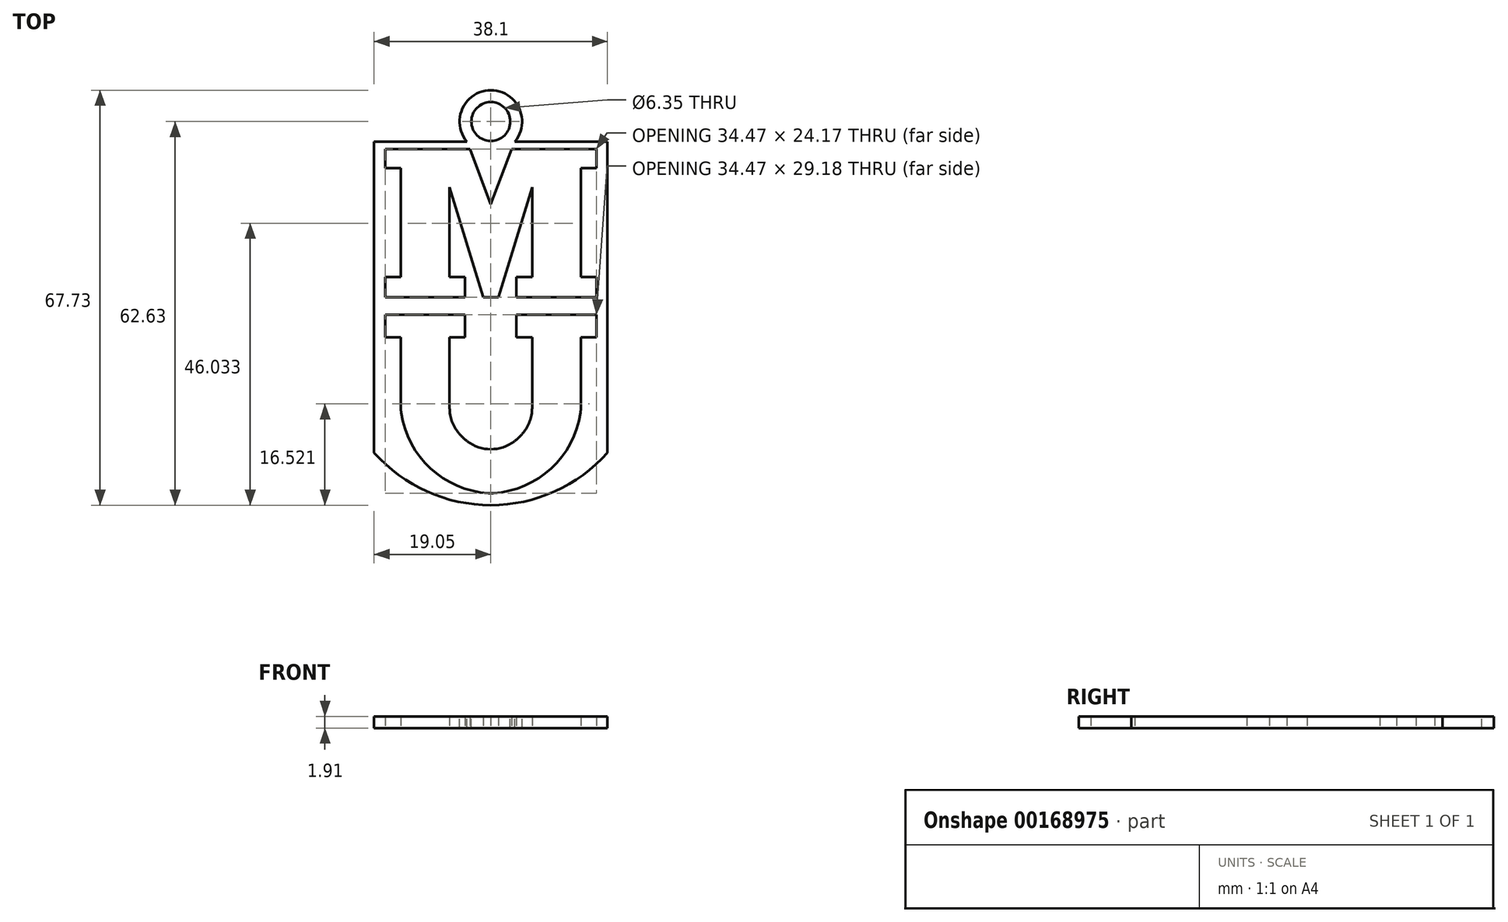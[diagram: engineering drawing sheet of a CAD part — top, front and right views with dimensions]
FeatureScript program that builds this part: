
annotation { "Feature Type Name" : "Feature", "Feature Type Description" : "" }
export const myFeature = defineFeature(function(context is Context, id is Id, definition is map)
    precondition{}
    {
        {
            var Q0;
            Q0=qCreatedBy(makeId("Top.planeOp"),FACE);
            var sketch = newSketch(context, id + "F0", { "sketchPlane" : qUnion([Q0])});
            skLineSegment(sketch, "E0.0.0", {"start": v(-17.24, 0) * mm, "end": v(-4.2, 0) * mm});
            skLineSegment(sketch, "E0.0.1", {"start": v(-4.2, 0) * mm, "end": v(-4.2, 3.32) * mm});
            skLineSegment(sketch, "E0.0.2", {"start": v(-4.2, 3.32) * mm, "end": v(-6.73, 3.32) * mm});
            skLineSegment(sketch, "E0.0.3", {"start": v(-6.73, 3.32) * mm, "end": v(-6.73, 17.94) * mm});
            skLineSegment(sketch, "E0.0.4", {"start": v(-6.73, 17.94) * mm, "end": v(-1.23, 0) * mm});
            skLineSegment(sketch, "E0.0.5", {"start": v(-1.23, 0) * mm, "end": v(1.23, 0) * mm});
            skLineSegment(sketch, "E0.0.6", {"start": v(1.23, 0) * mm, "end": v(6.73, 17.94) * mm});
            skLineSegment(sketch, "E0.0.7", {"start": v(6.73, 17.94) * mm, "end": v(6.73, 3.32) * mm});
            skLineSegment(sketch, "E0.0.8", {"start": v(6.73, 3.32) * mm, "end": v(4.2, 3.32) * mm});
            skLineSegment(sketch, "E0.0.9", {"start": v(4.2, 3.32) * mm, "end": v(4.2, 0) * mm});
            skLineSegment(sketch, "E0.0.10", {"start": v(4.2, 0) * mm, "end": v(17.24, 0) * mm});
            skLineSegment(sketch, "E0.0.11", {"start": v(17.24, 0) * mm, "end": v(17.24, 3.32) * mm});
            skLineSegment(sketch, "E0.0.12", {"start": v(17.24, 3.32) * mm, "end": v(14.7, 3.32) * mm});
            skLineSegment(sketch, "E0.0.13", {"start": v(14.7, 3.32) * mm, "end": v(14.7, 21.08) * mm});
            skLineSegment(sketch, "E0.0.14", {"start": v(14.7, 21.08) * mm, "end": v(17.24, 21.08) * mm});
            skLineSegment(sketch, "E0.0.15", {"start": v(17.24, 21.08) * mm, "end": v(17.24, 24.17) * mm});
            skLineSegment(sketch, "E0.0.16", {"start": v(17.24, 24.17) * mm, "end": v(3.4, 24.17) * mm});
            skLineSegment(sketch, "E0.0.17", {"start": v(3.4, 24.17) * mm, "end": v(0, 15.2) * mm});
            skLineSegment(sketch, "E0.0.18", {"start": v(0, 15.2) * mm, "end": v(-3.4, 24.17) * mm});
            skLineSegment(sketch, "E0.0.19", {"start": v(-3.4, 24.17) * mm, "end": v(-17.24, 24.17) * mm});
            skLineSegment(sketch, "E0.0.20", {"start": v(-17.24, 24.17) * mm, "end": v(-17.24, 21.08) * mm});
            skLineSegment(sketch, "E0.0.21", {"start": v(-17.24, 21.08) * mm, "end": v(-14.7, 21.08) * mm});
            skLineSegment(sketch, "E0.0.22", {"start": v(-14.7, 21.08) * mm, "end": v(-14.7, 3.32) * mm});
            skLineSegment(sketch, "E0.0.23", {"start": v(-14.7, 3.32) * mm, "end": v(-17.24, 3.32) * mm});
            skLineSegment(sketch, "E0.0.24", {"start": v(-17.24, 3.32) * mm, "end": v(-17.24, 0) * mm});
            skLineSegment(sketch, "E1.0.0", {"start": v(-4.2, -2.84) * mm, "end": v(-17.24, -2.84) * mm});
            skLineSegment(sketch, "E1.0.1", {"start": v(-17.24, -2.84) * mm, "end": v(-17.24, -6.53) * mm});
            skLineSegment(sketch, "E1.0.2", {"start": v(-17.24, -6.53) * mm, "end": v(-14.7, -6.53) * mm});
            skLineSegment(sketch, "E1.0.3", {"start": v(-14.7, -6.53) * mm, "end": v(-14.7, -17.95) * mm});
            skArc(sketch, "E1.0.4", {"start": v(-14.7, -17.95) * mm, "mid": v(-14.68, -18.4) * mm, "end": v(-14.63, -18.87) * mm});
            skArc(sketch, "E1.0.5", {"start": v(-14.63, -18.87) * mm, "mid": v(-9.85, -27.95) * mm, "end": v(-0.42, -32) * mm});
            skArc(sketch, "E1.0.6", {"start": v(-0.42, -32) * mm, "mid": v(0, -32.02) * mm, "end": v(0.42, -32) * mm});
            skArc(sketch, "E1.0.7", {"start": v(0.42, -32) * mm, "mid": v(9.85, -27.95) * mm, "end": v(14.63, -18.87) * mm});
            skArc(sketch, "E1.0.8", {"start": v(14.63, -18.87) * mm, "mid": v(14.68, -18.4) * mm, "end": v(14.7, -17.95) * mm});
            skLineSegment(sketch, "E1.0.9", {"start": v(14.7, -17.95) * mm, "end": v(14.7, -6.53) * mm});
            skLineSegment(sketch, "E1.0.10", {"start": v(14.7, -6.53) * mm, "end": v(17.24, -6.53) * mm});
            skLineSegment(sketch, "E1.0.11", {"start": v(17.24, -6.53) * mm, "end": v(17.24, -2.84) * mm});
            skLineSegment(sketch, "E1.0.12", {"start": v(17.24, -2.84) * mm, "end": v(4.2, -2.84) * mm});
            skLineSegment(sketch, "E1.0.13", {"start": v(4.2, -2.84) * mm, "end": v(4.2, -6.53) * mm});
            skLineSegment(sketch, "E1.0.14", {"start": v(4.2, -6.53) * mm, "end": v(6.73, -6.53) * mm});
            skLineSegment(sketch, "E1.0.15", {"start": v(6.73, -6.53) * mm, "end": v(6.73, -18.11) * mm});
            skArc(sketch, "E1.0.16", {"start": v(6.73, -18.11) * mm, "mid": v(6.35, -20.29) * mm, "end": v(5.24, -22.2) * mm});
            skArc(sketch, "E1.0.17", {"start": v(5.24, -22.2) * mm, "mid": v(4.57, -22.9) * mm, "end": v(3.83, -23.54) * mm});
            skArc(sketch, "E1.0.18", {"start": v(3.83, -23.54) * mm, "mid": v(0, -24.82) * mm, "end": v(-3.83, -23.54) * mm});
            skArc(sketch, "E1.0.19", {"start": v(-3.83, -23.54) * mm, "mid": v(-4.57, -22.9) * mm, "end": v(-5.24, -22.2) * mm});
            skArc(sketch, "E1.0.20", {"start": v(-5.24, -22.2) * mm, "mid": v(-6.35, -20.29) * mm, "end": v(-6.73, -18.11) * mm});
            skLineSegment(sketch, "E1.0.21", {"start": v(-6.73, -18.11) * mm, "end": v(-6.73, -6.53) * mm});
            skLineSegment(sketch, "E1.0.22", {"start": v(-6.73, -6.53) * mm, "end": v(-4.2, -6.53) * mm});
            skLineSegment(sketch, "E1.0.23", {"start": v(-4.2, -6.53) * mm, "end": v(-4.2, -2.84) * mm});
            skLineSegment(sketch, "E2.bottom", {"start": v(19.05, 25.4) * mm, "end": v(-19.05, 25.4) * mm});
            skLineSegment(sketch, "E2.left", {"start": v(19.05, 25.4) * mm, "end": v(19.05, -25.4) * mm});
            skLineSegment(sketch, "E2.right", {"start": v(-19.05, 25.4) * mm, "end": v(-19.05, -25.4) * mm});
            skPoint(sketch, "E2.middle", {"position": v(0, 0) * mm});
            skArc(sketch, "E3", {"start": v(-19.05, -25.4) * mm, "mid": v(0, -33.95) * mm, "end": v(19.05, -25.4) * mm});
            skSolve(sketch);
        }
        {
            var Q0;
            Q0 = qSketchRegion(id + "F0", true);
            extrude(context, id + "F1", {"entities" : qUnion([Q0]), "depth" : 1.9 * mm});
        }
        {
            var Q0;
            Q0=makeQuery(id+"F1.opExtrude","CAP_FACE",FACE,{"disambiguationData":[OSD([sQuery(id+"F0.wireOp",EDGE,"E0.0.0"),sQuery(id+"F0.wireOp",EDGE,"E0.0.1"),sQuery(id+"F0.wireOp",EDGE,"E0.0.2"),sQuery(id+"F0.wireOp",EDGE,"E0.0.3"),sQuery(id+"F0.wireOp",EDGE,"E0.0.4"),sQuery(id+"F0.wireOp",EDGE,"E0.0.5"),sQuery(id+"F0.wireOp",EDGE,"E0.0.6"),sQuery(id+"F0.wireOp",EDGE,"E0.0.7"),sQuery(id+"F0.wireOp",EDGE,"E0.0.8"),sQuery(id+"F0.wireOp",EDGE,"E0.0.9"),sQuery(id+"F0.wireOp",EDGE,"E0.0.10"),sQuery(id+"F0.wireOp",EDGE,"E0.0.11"),sQuery(id+"F0.wireOp",EDGE,"E0.0.12"),sQuery(id+"F0.wireOp",EDGE,"E0.0.13"),sQuery(id+"F0.wireOp",EDGE,"E0.0.14"),sQuery(id+"F0.wireOp",EDGE,"E0.0.15"),sQuery(id+"F0.wireOp",EDGE,"E0.0.16"),sQuery(id+"F0.wireOp",EDGE,"E0.0.17"),sQuery(id+"F0.wireOp",EDGE,"E0.0.18"),sQuery(id+"F0.wireOp",EDGE,"E0.0.19"),sQuery(id+"F0.wireOp",EDGE,"E0.0.20"),sQuery(id+"F0.wireOp",EDGE,"E0.0.21"),sQuery(id+"F0.wireOp",EDGE,"E0.0.22"),sQuery(id+"F0.wireOp",EDGE,"E0.0.23"),sQuery(id+"F0.wireOp",EDGE,"E0.0.24"),sQuery(id+"F0.wireOp",EDGE,"E1.0.0"),sQuery(id+"F0.wireOp",EDGE,"E1.0.1"),sQuery(id+"F0.wireOp",EDGE,"E1.0.2"),sQuery(id+"F0.wireOp",EDGE,"E1.0.3"),sQuery(id+"F0.wireOp",EDGE,"E1.0.4"),sQuery(id+"F0.wireOp",EDGE,"E1.0.5"),sQuery(id+"F0.wireOp",EDGE,"E1.0.6"),sQuery(id+"F0.wireOp",EDGE,"E1.0.7"),sQuery(id+"F0.wireOp",EDGE,"E1.0.8"),sQuery(id+"F0.wireOp",EDGE,"E1.0.9"),sQuery(id+"F0.wireOp",EDGE,"E1.0.10"),sQuery(id+"F0.wireOp",EDGE,"E1.0.11"),sQuery(id+"F0.wireOp",EDGE,"E1.0.12"),sQuery(id+"F0.wireOp",EDGE,"E1.0.13"),sQuery(id+"F0.wireOp",EDGE,"E1.0.14"),sQuery(id+"F0.wireOp",EDGE,"E1.0.15"),sQuery(id+"F0.wireOp",EDGE,"E1.0.16"),sQuery(id+"F0.wireOp",EDGE,"E1.0.17"),sQuery(id+"F0.wireOp",EDGE,"E1.0.18"),sQuery(id+"F0.wireOp",EDGE,"E1.0.19"),sQuery(id+"F0.wireOp",EDGE,"E1.0.20"),sQuery(id+"F0.wireOp",EDGE,"E1.0.21"),sQuery(id+"F0.wireOp",EDGE,"E1.0.22"),sQuery(id+"F0.wireOp",EDGE,"E1.0.23"),sQuery(id+"F0.wireOp",EDGE,"E2.bottom"),sQuery(id+"F0.wireOp",EDGE,"E2.left"),sQuery(id+"F0.wireOp",EDGE,"E2.right"),sQuery(id+"F0.wireOp",EDGE,"E3")])],"isStart":false});
            var sketch = newSketch(context, id + "F2", { "sketchPlane" : qUnion([Q0])});
            skCircle(sketch, "E4", {"center": v(0, 28.68) * mm, "radius": 3.18 * mm});
            skCircle(sketch, "E5", {"center": v(0, 28.68) * mm, "radius": 5.1 * mm});
            skSolve(sketch);
        }
        {
            var Q0;
            Q0 = qSketchRegion(id + "F2", true);
            extrude(context, id + "F3", {"entities" : qUnion([Q0]), "operationType" : NewBodyOperationType.ADD, "oppositeDirection" : true, "depth" : 1.9 * mm});
        }
    });
